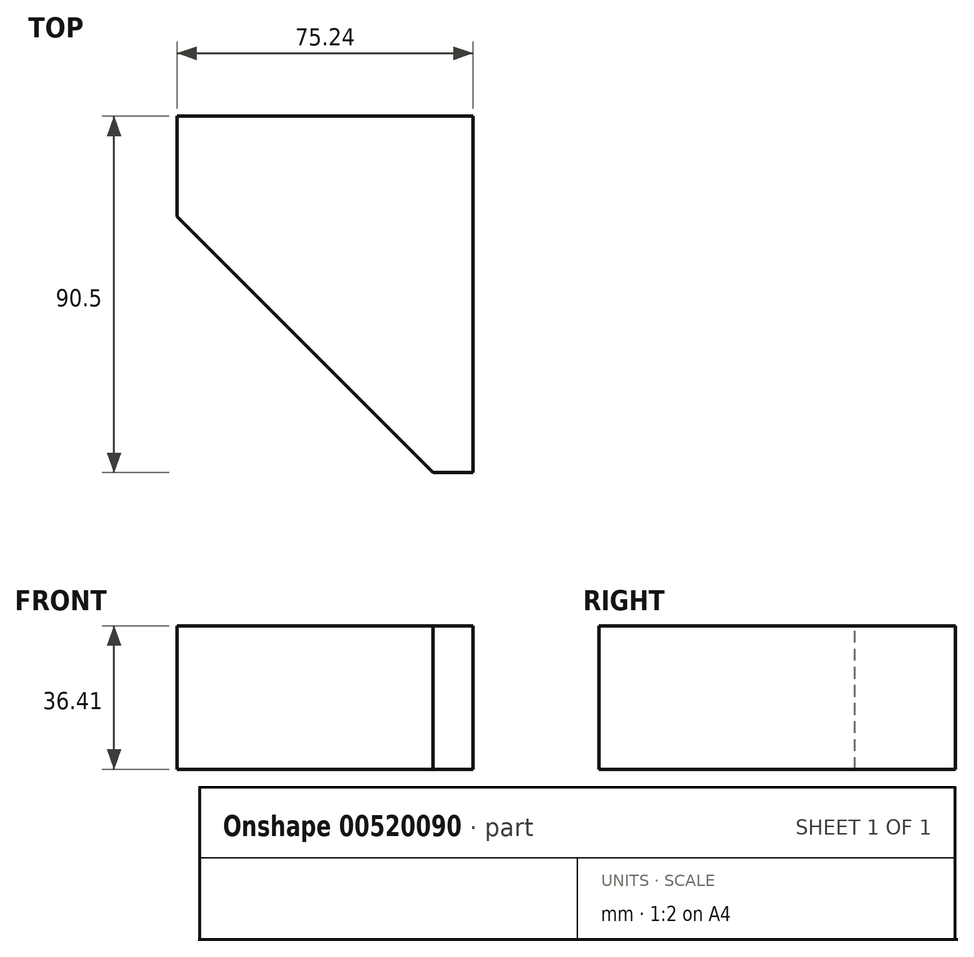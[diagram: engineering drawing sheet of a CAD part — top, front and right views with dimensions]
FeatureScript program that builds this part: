
annotation { "Feature Type Name" : "Feature", "Feature Type Description" : "" }
export const myFeature = defineFeature(function(context is Context, id is Id, definition is map)
    precondition{}
    {
        {
            var Q0;
            Q0=qCreatedBy(makeId("Front.planeOp"),FACE);
            var sketch = newSketch(context, id + "F0", { "sketchPlane" : qUnion([Q0])});
            skLineSegment(sketch, "E0.bottom", {"start": v(0, 0) * mm, "end": v(75.24, 0) * mm});
            skLineSegment(sketch, "E0.top", {"start": v(0, 36.41) * mm, "end": v(75.24, 36.41) * mm});
            skLineSegment(sketch, "E0.left", {"start": v(0, 0) * mm, "end": v(0, 36.41) * mm});
            skLineSegment(sketch, "E0.right", {"start": v(75.24, 0) * mm, "end": v(75.24, 36.41) * mm});
            skSolve(sketch);
        }
        {
            var Q0;
            Q0 = qSketchRegion(id + "F0", true);
            extrude(context, id + "F1", {"entities" : qUnion([Q0]), "depth" : 90.5 * mm, "offsetDistance" : 25 * mm});
        }
        {
            var Q0;
            Q0=makeQuery(id+"F1.opExtrude","CAP_EDGE",EDGE,{"disambiguationData":[OSD([sQuery(id+"F0.wireOp",EDGE,"E0.left")])],"isStart":false});
            chamfer(context, id + "F2", {"entities" : qUnion([Q0]), "width" : 65 * mm, "tangentPropagation" : true});
        }
    });
